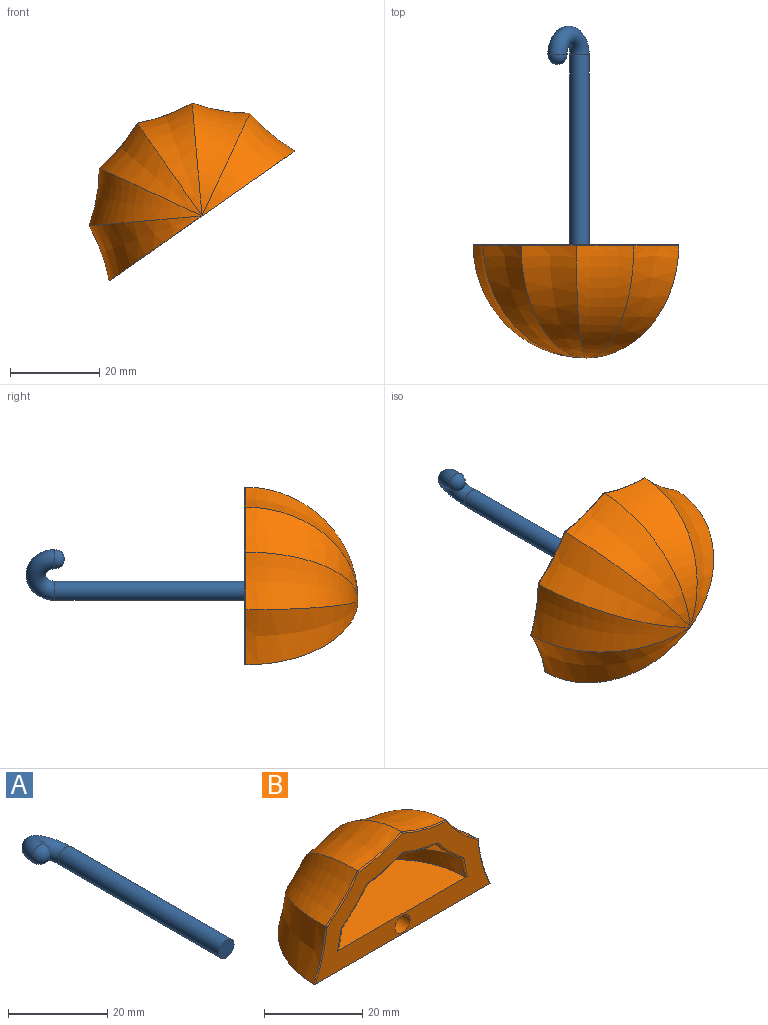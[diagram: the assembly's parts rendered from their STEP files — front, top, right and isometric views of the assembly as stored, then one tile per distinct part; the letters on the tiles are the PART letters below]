
ASSEMBLY  parts=2 mates=1
PART A: 4 faces, bbox 12.5x52.7x9 mm
  f0: cylinder r=2.16mm len=45.72mm, axis (0,-1,0), area 620.2mm2, adj f1,f2
  f1: plane 4.32x4.32mm, normal (0,-1,0), area 14.6mm2, adj f0
  f2: torus R=4.32mm, axis (-0.5,0,-0.87), area 184mm2, adj f0,f3
  f3: sphere r=2.16mm, area 29.3mm2, adj f2
PART B: 31 faces, bbox 62.9x35.6x38.7 mm
  f0: plane 50.25x25.13mm, normal (0,-1,0), area 489.8mm2, adj f1,f8,f9,f10,f11,f12,f13,f14
  f1: bspline ~10.25x10.21mm, area 8.2mm2, adj f0,f2,f8,f13
  f2: offset ~34.71x28.87mm, area 184.3mm2, adj f1,f3,f7,f12
  f3: offset ~35.4x32.68mm, area 195mm2, adj f2,f4,f8,f12
  f4: offset ~35.4x32.68mm, area 195mm2, adj f3,f5,f9,f12
  f5: offset ~34.71x28.87mm, area 184.3mm2, adj f4,f6,f10,f12
  f6: offset ~34.26x26.79mm, area 45.7mm2, adj f5,f11,f12
  f7: offset ~34.26x26.79mm, area 45.7mm2, adj f2,f12,f13
  f8: bspline ~13.63x4.07mm, area 8.2mm2, adj f0,f1,f3,f9
  f9: bspline ~13.63x4.07mm, area 8.2mm2, adj f0,f4,f8,f10
  f10: bspline ~10.25x10.21mm, area 8.2mm2, adj f0,f5,f9,f11
  f11: bspline ~7.96x2.09mm, area 4mm2, adj f0,f6,f10,f12
  f12: plane 40.51x22.75mm, normal (0,0,1), area 565.6mm2, adj f0,f2,f3,f4,f5,f6,f7,f11
  f13: bspline ~7.96x2.09mm, area 4mm2, adj f0,f1,f7,f12
  f14: bspline ~15.39x4.67mm, area 5.3mm2, adj f0,f15,f23,f28
  f15: bspline ~22.04x14.38mm, area 123.3mm2, adj f14,f16,f28
  f16: bspline ~25.4x22mm, area 208.3mm2, adj f15,f17,f18,f22,f23
  f17: bspline ~19.14x9.57mm, area 31.5mm2, adj f16,f28
  f18: bspline ~22.04x14.38mm, area 123.3mm2, adj f16,f19,f24
  f19: bspline ~25.4x25.14mm, area 208.3mm2, adj f18,f20,f22,f25
  f20: bspline ~25.4x22mm, area 208.3mm2, adj f19,f21,f26
  f21: bspline ~25.4x25.4mm, area 208.3mm2, adj f20,f27,f28
  f22: bspline ~19.14x9.57mm, area 31.5mm2, adj f16,f19
  f23: bspline ~11.67x11.23mm, area 5.3mm2, adj f0,f14,f16,f24
  f24: bspline ~15.39x4.67mm, area 5.3mm2, adj f0,f18,f23,f25
  f25: bspline ~15.39x4.67mm, area 5.3mm2, adj f0,f19,f24,f26
  f26: bspline ~11.67x11.23mm, area 5.3mm2, adj f0,f20,f25,f27
  f27: bspline ~15.39x4.67mm, area 5.3mm2, adj f0,f21,f26,f28
  f28: plane 60.16x34.76mm, normal (0,0,-1), area 1013.4mm2, adj f0,f14,f15,f17,f21,f27
  f29: cylinder r=2.18mm len=7.62mm, axis (0,-1,0), area 104.3mm2, adj f0,f30
  f30: plane 4.36x4.36mm, normal (0,-1,0), area 14.9mm2, adj f29
PLACE A rot(axis=(0,1,0),25deg) t=(50.29,1.05,-26.9)mm
PLACE B rot(axis=(-0.3,0,0.95),180deg) t=(27.41,4.23,5.78)mm
MATE cylindrical B.f29 <-> A.f0  axis (0,1,0) through (25.96,-3.39,7.85)mm
